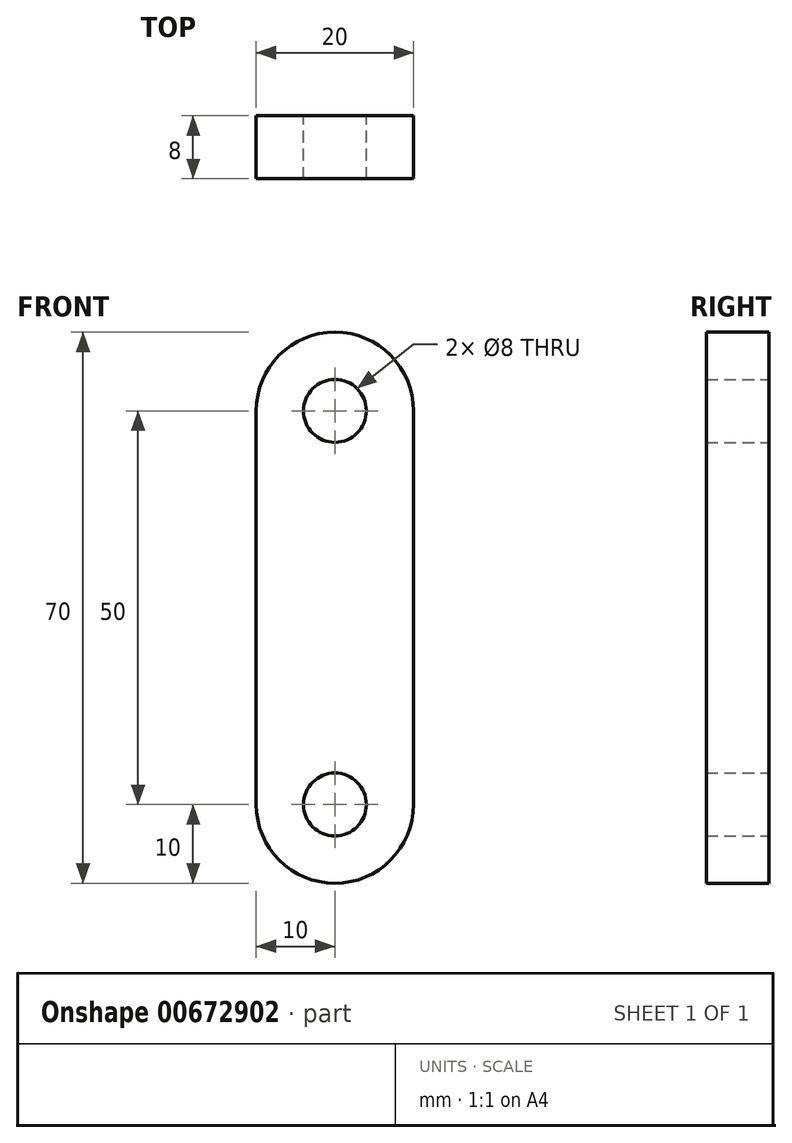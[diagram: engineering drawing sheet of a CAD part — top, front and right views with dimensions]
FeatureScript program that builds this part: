
annotation { "Feature Type Name" : "Feature", "Feature Type Description" : "" }
export const myFeature = defineFeature(function(context is Context, id is Id, definition is map)
    precondition{}
    {
        {
            var Q0;
            Q0=qCreatedBy(makeId("Front.planeOp"),FACE);
            var sketch = newSketch(context, id + "F0", { "sketchPlane" : qUnion([Q0])});
            skArc(sketch, "E0", {"start": v(-10, 0) * mm, "mid": v(0, -10) * mm, "end": v(10, 0) * mm});
            skArc(sketch, "E1", {"start": v(10, 50) * mm, "mid": v(0, 60) * mm, "end": v(-10, 50) * mm});
            skLineSegment(sketch, "E2", {"start": v(-10, 50) * mm, "end": v(-10, 0) * mm});
            skLineSegment(sketch, "E3", {"start": v(10, 50) * mm, "end": v(10, 0) * mm});
            skCircle(sketch, "E4", {"center": v(0, 50) * mm, "radius": 4 * mm});
            skCircle(sketch, "E5", {"center": v(0, 0) * mm, "radius": 4 * mm});
            skSolve(sketch);
        }
        {
            var Q0;
            Q0 = qSketchRegion(id + "F0", true);
            extrude(context, id + "F1", {"entities" : qUnion([Q0]), "depth" : 8 * mm, "offsetDistance" : 25 * mm});
        }
    });
